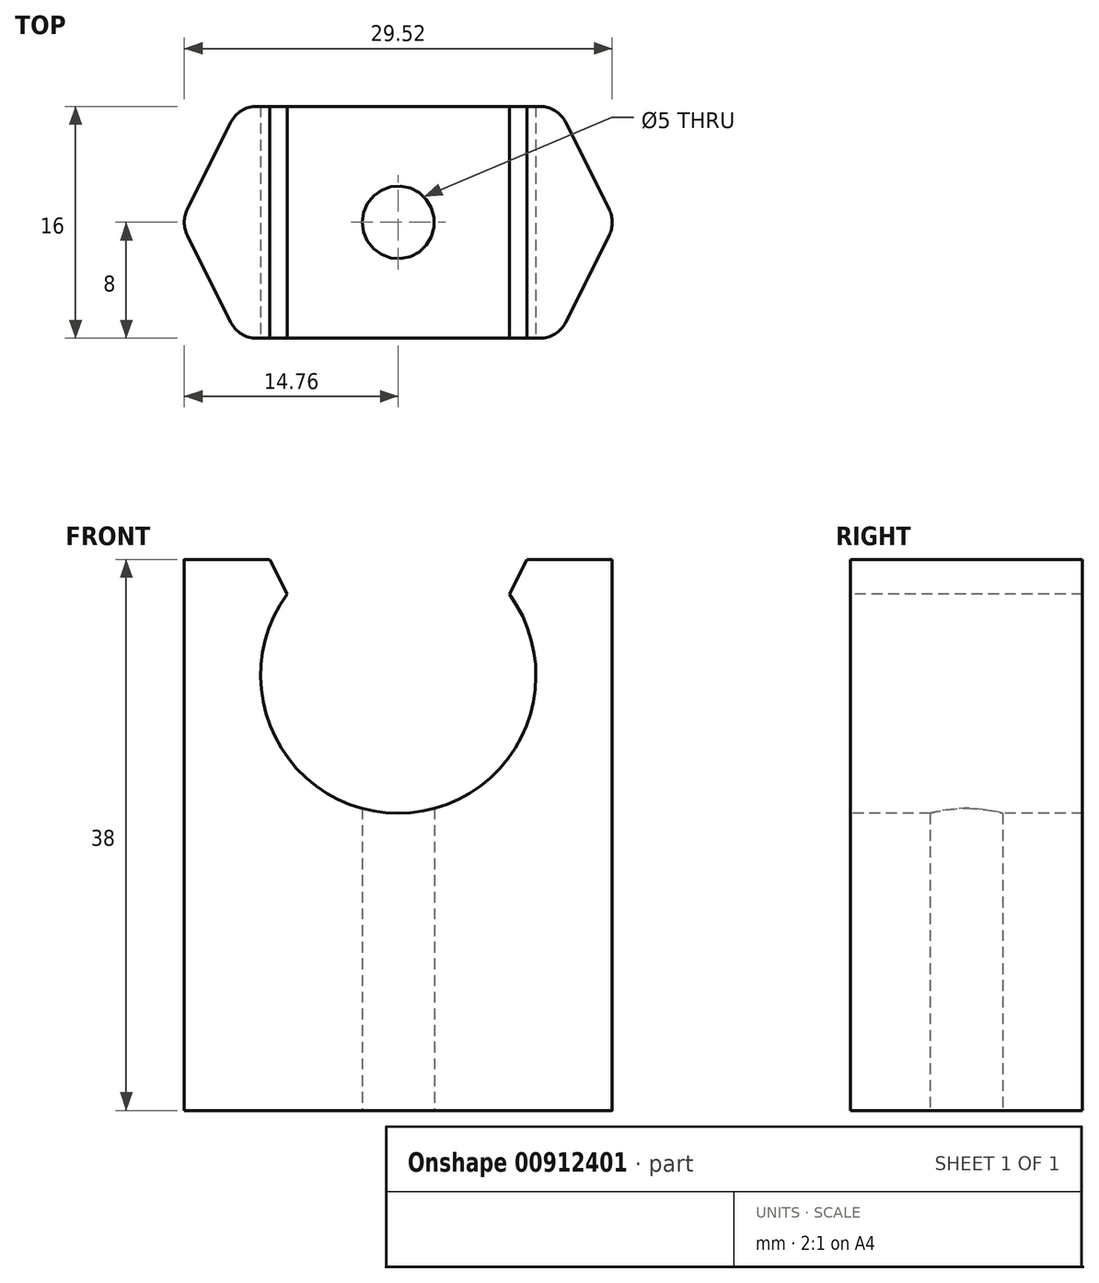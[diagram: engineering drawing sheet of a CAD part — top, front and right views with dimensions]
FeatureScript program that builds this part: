
annotation { "Feature Type Name" : "Feature", "Feature Type Description" : "" }
export const myFeature = defineFeature(function(context is Context, id is Id, definition is map)
    precondition{}
    {
        {
            var Q0;
            Q0=qCreatedBy(makeId("Top.planeOp"),FACE);
            var sketch = newSketch(context, id + "F0", { "sketchPlane" : qUnion([Q0])});
            skLineSegment(sketch, "E0.bottom", {"start": v(-11, 8) * mm, "end": v(11, 8) * mm});
            skLineSegment(sketch, "E0.top", {"start": v(-11, -8) * mm, "end": v(11, -8) * mm});
            skLineSegment(sketch, "E1", {"start": v(11, 8) * mm, "end": v(15, 0) * mm});
            skLineSegment(sketch, "E2", {"start": v(15, 0) * mm, "end": v(11, -8) * mm});
            skLineSegment(sketch, "E3", {"start": v(-11, 8) * mm, "end": v(-15, 0) * mm});
            skLineSegment(sketch, "E4", {"start": v(-15, 0) * mm, "end": v(-11, -8) * mm});
            skCircle(sketch, "E5", {"center": v(0, 0) * mm, "radius": 2.5 * mm});
            skSolve(sketch);
        }
        {
            var Q0;
            Q0 = qSketchRegion(id + "F0", true);
            extrude(context, id + "F1", {"entities" : qUnion([Q0]), "depth" : 20 * mm, "offsetDistance" : 25 * mm});
        }
        {
            var Q0;
            Q0=makeQuery(id+"F1.opExtrude","CAP_FACE",FACE,{"disambiguationData":[OSD([sQuery(id+"F0.wireOp",EDGE,"E0.bottom"),sQuery(id+"F0.wireOp",EDGE,"E0.top"),sQuery(id+"F0.wireOp",EDGE,"E1"),sQuery(id+"F0.wireOp",EDGE,"E2"),sQuery(id+"F0.wireOp",EDGE,"E3"),sQuery(id+"F0.wireOp",EDGE,"E4"),sQuery(id+"F0.wireOp",EDGE,"E5")])],"isStart":false});
            extrude(context, id + "F2", {"entities" : qUnion([Q0]), "operationType" : NewBodyOperationType.ADD, "depth" : 18 * mm, "offsetDistance" : 25 * mm});
        }
        {
            var Q0;
            Q0=qCreatedBy(makeId("Front.planeOp"),FACE);
            var sketch = newSketch(context, id + "F3", { "sketchPlane" : qUnion([Q0])});
            skArc(sketch, "E6", {"start": v(-5, 38.08) * mm, "mid": v(0, 20.5) * mm, "end": v(5, 38.08) * mm});
            skLineSegment(sketch, "E7", {"start": v(-5, 38.08) * mm, "end": v(5, 38.08) * mm});
            skSolve(sketch);
        }
        {
            var Q0;
            Q0 = qSketchRegion(id + "F3", true);
            extrude(context, id + "F4", {"entities" : qUnion([Q0]), "operationType" : NewBodyOperationType.REMOVE, "endBound" : BoundingType.SYMMETRIC, "oppositeDirection" : true, "depth" : 25 * mm, "offsetDistance" : 25 * mm});
        }
        {
            var Q0;
            {var subQ0=sQuery(id+"F0.wireOp",EDGE,"E2");var subQ1=sQuery(id+"F0.wireOp",EDGE,"E0.top");Q0=makeQuery(id+"F2.boolean.opBoolean","MERGE",EDGE,{"derivedFrom":[makeQuery(id+"F1.opExtrude","SWEPT_EDGE",EDGE,{"disambiguationData":[OSD([subQ1,subQ0])]}),makeQuery(id+"F2.opExtrude","SWEPT_EDGE",EDGE,{"disambiguationData":[OSD([subQ1,subQ0])]})]});}
            var Q1;
            {var subQ0=sQuery(id+"F0.wireOp",EDGE,"E2");var subQ1=sQuery(id+"F0.wireOp",EDGE,"E1");Q1=makeQuery(id+"F2.boolean.opBoolean","MERGE",EDGE,{"derivedFrom":[makeQuery(id+"F1.opExtrude","SWEPT_EDGE",EDGE,{"disambiguationData":[OSD([subQ1,subQ0])]}),makeQuery(id+"F2.opExtrude","SWEPT_EDGE",EDGE,{"disambiguationData":[OSD([subQ1,subQ0])]})]});}
            var Q2;
            {var subQ0=sQuery(id+"F0.wireOp",EDGE,"E1");var subQ1=sQuery(id+"F0.wireOp",EDGE,"E0.bottom");Q2=makeQuery(id+"F2.boolean.opBoolean","MERGE",EDGE,{"derivedFrom":[makeQuery(id+"F1.opExtrude","SWEPT_EDGE",EDGE,{"disambiguationData":[OSD([subQ1,subQ0])]}),makeQuery(id+"F2.opExtrude","SWEPT_EDGE",EDGE,{"disambiguationData":[OSD([subQ1,subQ0])]})]});}
            var Q3;
            {var subQ0=sQuery(id+"F0.wireOp",EDGE,"E4");var subQ1=sQuery(id+"F0.wireOp",EDGE,"E0.top");Q3=makeQuery(id+"F2.boolean.opBoolean","MERGE",EDGE,{"derivedFrom":[makeQuery(id+"F1.opExtrude","SWEPT_EDGE",EDGE,{"disambiguationData":[OSD([subQ1,subQ0])]}),makeQuery(id+"F2.opExtrude","SWEPT_EDGE",EDGE,{"disambiguationData":[OSD([subQ1,subQ0])]})]});}
            var Q4;
            {var subQ0=sQuery(id+"F0.wireOp",EDGE,"E4");var subQ1=sQuery(id+"F0.wireOp",EDGE,"E3");Q4=makeQuery(id+"F2.boolean.opBoolean","MERGE",EDGE,{"derivedFrom":[makeQuery(id+"F1.opExtrude","SWEPT_EDGE",EDGE,{"disambiguationData":[OSD([subQ1,subQ0])]}),makeQuery(id+"F2.opExtrude","SWEPT_EDGE",EDGE,{"disambiguationData":[OSD([subQ1,subQ0])]})]});}
            var Q5;
            {var subQ0=sQuery(id+"F0.wireOp",EDGE,"E3");var subQ1=sQuery(id+"F0.wireOp",EDGE,"E0.bottom");Q5=makeQuery(id+"F2.boolean.opBoolean","MERGE",EDGE,{"derivedFrom":[makeQuery(id+"F1.opExtrude","SWEPT_EDGE",EDGE,{"disambiguationData":[OSD([subQ1,subQ0])]}),makeQuery(id+"F2.opExtrude","SWEPT_EDGE",EDGE,{"disambiguationData":[OSD([subQ1,subQ0])]})]});}
            fillet(context, id + "F5", {"entities" : qUnion([Q0, Q1, Q2, Q3, Q4, Q5]), "radius" : 2 * mm, "tangentPropagation" : true, "allowEdgeOverflow" : false});
        }
        {
            var Q0;
            Q0=makeQuery(id+"F4.boolean.opBoolean","INTERSECT",EDGE,{"disambiguationData":[OD(1.0)],"derivedFrom":[makeQuery(id+"F2.opExtrude","CAP_FACE",FACE,{"disambiguationData":[OSD([sQuery(id+"F0.wireOp",EDGE,"E0.bottom"),sQuery(id+"F0.wireOp",EDGE,"E0.top"),sQuery(id+"F0.wireOp",EDGE,"E1"),sQuery(id+"F0.wireOp",EDGE,"E2"),sQuery(id+"F0.wireOp",EDGE,"E3"),sQuery(id+"F0.wireOp",EDGE,"E4"),sQuery(id+"F0.wireOp",EDGE,"E5")])],"isStart":false}),makeQuery(id+"F4.opExtrude","SWEPT_FACE",FACE,{"disambiguationData":[OSD([sQuery(id+"F3.wireOp",EDGE,"E6")])]})]});
            var Q1;
            Q1=makeQuery(id+"F4.boolean.opBoolean","INTERSECT",EDGE,{"disambiguationData":[OD(0.0)],"derivedFrom":[makeQuery(id+"F2.opExtrude","CAP_FACE",FACE,{"disambiguationData":[OSD([sQuery(id+"F0.wireOp",EDGE,"E0.bottom"),sQuery(id+"F0.wireOp",EDGE,"E0.top"),sQuery(id+"F0.wireOp",EDGE,"E1"),sQuery(id+"F0.wireOp",EDGE,"E2"),sQuery(id+"F0.wireOp",EDGE,"E3"),sQuery(id+"F0.wireOp",EDGE,"E4"),sQuery(id+"F0.wireOp",EDGE,"E5")])],"isStart":false}),makeQuery(id+"F4.opExtrude","SWEPT_FACE",FACE,{"disambiguationData":[OSD([sQuery(id+"F3.wireOp",EDGE,"E6")])]})]});
            chamfer(context, id + "F6", {"entities" : qUnion([Q0, Q1]), "width" : 1.5 * mm, "tangentPropagation" : true});
        }
    });
